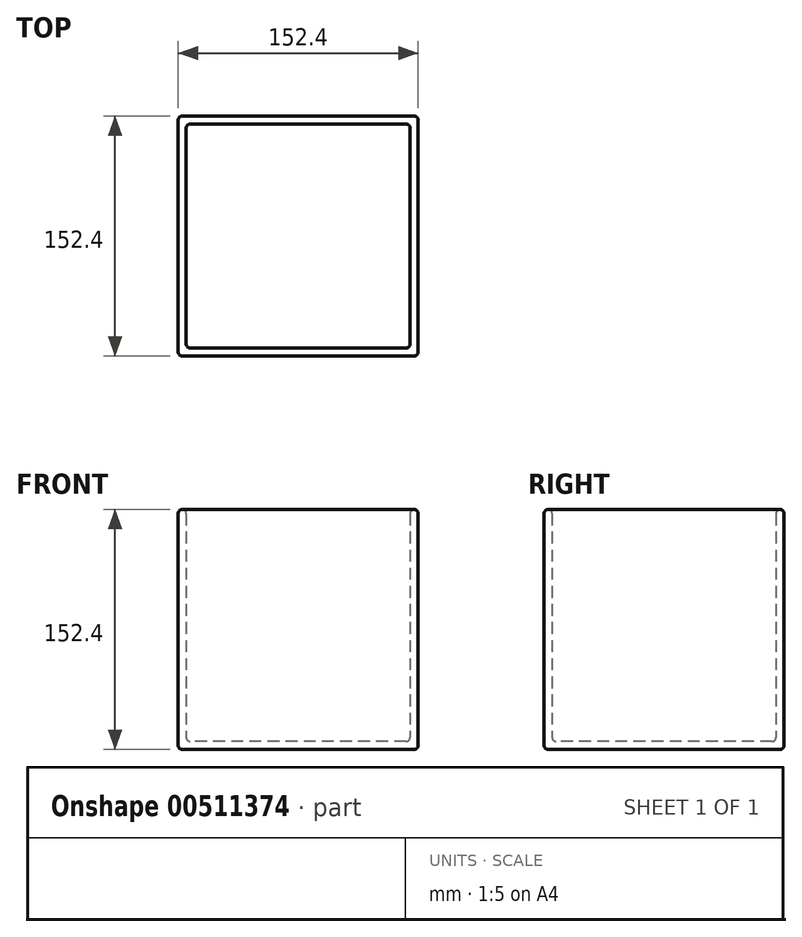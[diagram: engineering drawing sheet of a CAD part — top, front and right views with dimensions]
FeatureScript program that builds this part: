
annotation { "Feature Type Name" : "Feature", "Feature Type Description" : "" }
export const myFeature = defineFeature(function(context is Context, id is Id, definition is map)
    precondition{}
    {
        {
            var Q0;
            Q0=qCreatedBy(makeId("Top.planeOp"),FACE);
            var sketch = newSketch(context, id + "F0", { "sketchPlane" : qUnion([Q0])});
            skLineSegment(sketch, "E0.bottom", {"start": v(76.2, 76.2) * mm, "end": v(-76.2, 76.2) * mm});
            skLineSegment(sketch, "E0.top", {"start": v(76.2, -76.2) * mm, "end": v(-76.2, -76.2) * mm});
            skLineSegment(sketch, "E0.left", {"start": v(76.2, 76.2) * mm, "end": v(76.2, -76.2) * mm});
            skLineSegment(sketch, "E0.right", {"start": v(-76.2, 76.2) * mm, "end": v(-76.2, -76.2) * mm});
            skPoint(sketch, "E0.middle", {"position": v(0, 0) * mm});
            skSolve(sketch);
        }
        {
            var Q0;
            Q0=makeQuery(id+"F0.imprint","IMPRINT",FACE,{"disambiguationData":[TD([[makeQuery(id+"F0.imprint","IMPRINT",EDGE,{"derivedFrom":sQuery(id+"F0.wireOp",EDGE,"E0.bottom")}),1.0]])]});
            extrude(context, id + "F1", {"entities" : qUnion([Q0]), "depth" : 152.4 * mm});
        }
        {
            var Q0;
            Q0=makeQuery(id+"F1.opExtrude","CAP_FACE",FACE,{"disambiguationData":[OSD([sQuery(id+"F0.wireOp",EDGE,"E0.bottom"),sQuery(id+"F0.wireOp",EDGE,"E0.top"),sQuery(id+"F0.wireOp",EDGE,"E0.left"),sQuery(id+"F0.wireOp",EDGE,"E0.right")])],"isStart":false});
            shell(context, id + "F2", {"entities" : qUnion([Q0]), "thickness" : 5.08 * mm});
        }
        {
            var Q0;
            Q0=makeQuery(id+"F1.opExtrude","CAP_FACE",FACE,{"disambiguationData":[OSD([sQuery(id+"F0.wireOp",EDGE,"E0.bottom"),sQuery(id+"F0.wireOp",EDGE,"E0.top"),sQuery(id+"F0.wireOp",EDGE,"E0.left"),sQuery(id+"F0.wireOp",EDGE,"E0.right")])],"isStart":false});
            var Q1;
            Q1=makeQuery(id+"F1.opExtrude","SWEPT_FACE",FACE,{"disambiguationData":[OSD([sQuery(id+"F0.wireOp",EDGE,"E0.bottom")])]});
            var Q2;
            Q2=makeQuery(id+"F2.opShell","OFFSET_FACE",FACE,{"disambiguationData":[OSD([sQuery(id+"F0.wireOp",EDGE,"E0.bottom"),sQuery(id+"F0.wireOp",EDGE,"E0.top"),sQuery(id+"F0.wireOp",EDGE,"E0.left"),sQuery(id+"F0.wireOp",EDGE,"E0.right")])]});
            var Q3;
            Q3=makeQuery(id+"F2.opShell","OFFSET_FACE",FACE,{"disambiguationData":[OSD([sQuery(id+"F0.wireOp",EDGE,"E0.right")])]});
            var Q4;
            Q4=makeQuery(id+"F2.opShell","OFFSET_FACE",FACE,{"disambiguationData":[OSD([sQuery(id+"F0.wireOp",EDGE,"E0.top")])]});
            var Q5;
            Q5=makeQuery(id+"F2.opShell","OFFSET_FACE",FACE,{"disambiguationData":[OSD([sQuery(id+"F0.wireOp",EDGE,"E0.bottom")])]});
            var Q6;
            Q6=makeQuery(id+"F1.opExtrude","SWEPT_FACE",FACE,{"disambiguationData":[OSD([sQuery(id+"F0.wireOp",EDGE,"E0.right")])]});
            var Q7;
            Q7=makeQuery(id+"F1.opExtrude","SWEPT_FACE",FACE,{"disambiguationData":[OSD([sQuery(id+"F0.wireOp",EDGE,"E0.top")])]});
            var Q8;
            Q8=makeQuery(id+"F1.opExtrude","CAP_FACE",FACE,{"disambiguationData":[OSD([sQuery(id+"F0.wireOp",EDGE,"E0.bottom"),sQuery(id+"F0.wireOp",EDGE,"E0.top"),sQuery(id+"F0.wireOp",EDGE,"E0.left"),sQuery(id+"F0.wireOp",EDGE,"E0.right")])],"isStart":true});
            fillet(context, id + "F3", {"entities" : qUnion([Q0, Q1, Q2, Q3, Q4, Q5, Q6, Q7, Q8]), "radius" : 2.54 * mm, "tangentPropagation" : true, "allowEdgeOverflow" : false});
        }
    });
